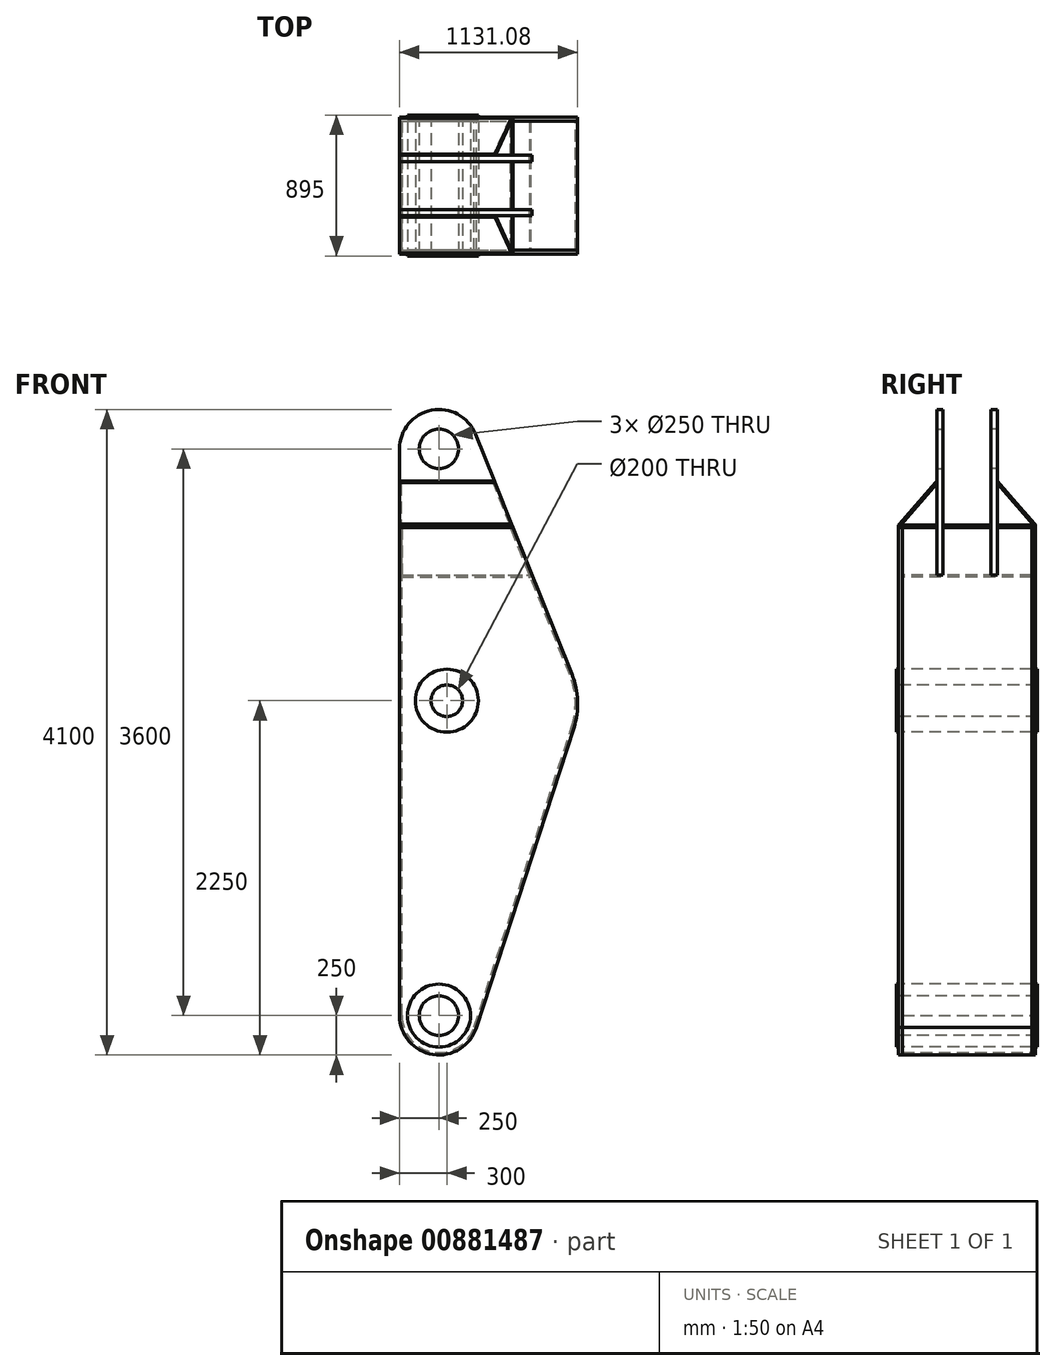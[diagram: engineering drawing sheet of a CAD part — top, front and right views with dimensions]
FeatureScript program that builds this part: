
annotation { "Feature Type Name" : "Feature", "Feature Type Description" : "" }
export const myFeature = defineFeature(function(context is Context, id is Id, definition is map)
    precondition{}
    {
        {
            var Q0;
            Q0=qCreatedBy(makeId("Front.planeOp"),FACE);
            var sketch = newSketch(context, id + "F0", { "sketchPlane" : qUnion([Q0])});
            skArc(sketch, "E0", {"start": v(-250, 0) * mm, "mid": v(-37.8, -247.13) * mm, "end": v(238.57, -74.73) * mm});
            skCircle(sketch, "E1", {"center": v(0, 0) * mm, "radius": 125 * mm});
            skCircle(sketch, "E2", {"center": v(0, 0) * mm, "radius": 200 * mm});
            skLineSegment(sketch, "E3", {"start": v(-250, 0) * mm, "end": v(-250, 3600) * mm});
            skCircle(sketch, "E4", {"center": v(0, 3600) * mm, "radius": 125 * mm});
            skLineSegment(sketch, "E5", {"start": v(238.57, -74.73) * mm, "end": v(856.6, 1827.38) * mm});
            skLineSegment(sketch, "E6", {"start": v(844.99, 2168.4) * mm, "end": v(231.96, 3693.25) * mm});
            skCircle(sketch, "E7", {"center": v(50, 2000) * mm, "radius": 100 * mm});
            skCircle(sketch, "E8", {"center": v(50, 2000) * mm, "radius": 200 * mm});
            skPoint(sketch, "E9.visualSharp", {"position": v(912.7, 2000) * mm});
            skArc(sketch, "E9.filletArc", {"start": v(856.6, 1827.38) * mm, "mid": v(880.79, 1998.91) * mm, "end": v(844.99, 2168.4) * mm});
            skArc(sketch, "E10", {"start": v(231.96, 3693.25) * mm, "mid": v(-47.5, 3845.45) * mm, "end": v(-250, 3600) * mm});
            skLineSegment(sketch, "E11", {"start": v(-250, 3100) * mm, "end": v(470.46, 3100) * mm});
            skLineSegment(sketch, "E12", {"start": v(-250, 2800) * mm, "end": v(591.07, 2800) * mm});
            skSolve(sketch);
        }
        {
            var Q0;
            {var subQ1=sQuery(id+"F0.wireOp",EDGE,"E0");Q0=makeQuery(id+"F0.imprint","IMPRINT",FACE,{"disambiguationData":[TD([[makeQuery(id+"F0.imprint","IMPRINT",EDGE,{"derivedFrom":subQ1}),1.0]])]});}
            var Q1;
            {var subQ0=sQuery(id+"F0.wireOp",EDGE,"E11");Q1=makeQuery(id+"F0.imprint","IMPRINT",FACE,{"disambiguationData":[TD([[makeQuery(id+"F0.imprint","IMPRINT",EDGE,{"derivedFrom":subQ0}),-1.0]])]});}
            extrude(context, id + "F1", {"entities" : qUnion([Q0, Q1]), "depth" : 25 * mm, "offsetDistance" : 25 * mm, "symmetric" : true});
        }
        {
            var Q0;
            Q0=makeQuery(id+"F1.opExtrude","CAP_FACE",FACE,{"disambiguationData":[OSD([sQuery(id+"F0.wireOp",EDGE,"E0"),sQuery(id+"F0.wireOp",EDGE,"E2"),sQuery(id+"F0.wireOp",EDGE,"E3"),sQuery(id+"F0.wireOp",EDGE,"E5"),sQuery(id+"F0.wireOp",EDGE,"E6"),sQuery(id+"F0.wireOp",EDGE,"E8"),sQuery(id+"F0.wireOp",EDGE,"E9.filletArc"),sQuery(id+"F0.wireOp",EDGE,"E11")])],"isStart":true});
            cPlane(context, id + "F2", {"entities" : qUnion([Q0]), "cplaneType" : CPlaneType.OFFSET, "offset" : 410 * mm, "width" : 150 * mm, "height" : 150 * mm});
        }
        {
            var Q0;
            Q0=makeQuery(id+"F1.opExtrude","SWEPT_BODY",BODY,{"disambiguationData":[OSD([sQuery(id+"F0.wireOp",EDGE,"E0"),sQuery(id+"F0.wireOp",EDGE,"E2"),sQuery(id+"F0.wireOp",EDGE,"E3"),sQuery(id+"F0.wireOp",EDGE,"E5"),sQuery(id+"F0.wireOp",EDGE,"E6"),sQuery(id+"F0.wireOp",EDGE,"E8"),sQuery(id+"F0.wireOp",EDGE,"E9.filletArc"),sQuery(id+"F0.wireOp",EDGE,"E11")])]});
            var Q1;
            Q1=qCreatedBy(id+"F2.planeOp",FACE);
            mirror(context, id + "F3", {"entities" : qUnion([Q0]), "mirrorPlane" : qUnion([Q1])});
        }
        {
            var Q0;
            Q0=makeQuery(id+"F3.opPattern","COPY",FACE,{"derivedFrom":makeQuery(id+"F1.opExtrude","CAP_FACE",FACE,{"disambiguationData":[OSD([sQuery(id+"F0.wireOp",EDGE,"E0"),sQuery(id+"F0.wireOp",EDGE,"E2"),sQuery(id+"F0.wireOp",EDGE,"E3"),sQuery(id+"F0.wireOp",EDGE,"E5"),sQuery(id+"F0.wireOp",EDGE,"E6"),sQuery(id+"F0.wireOp",EDGE,"E8"),sQuery(id+"F0.wireOp",EDGE,"E9.filletArc"),sQuery(id+"F0.wireOp",EDGE,"E11")])],"isStart":true}),"instanceName":"1"});
            var Q1;
            Q1=makeQuery(id+"F3.opPattern","COPY",FACE,{"derivedFrom":makeQuery(id+"F1.opExtrude","CAP_FACE",FACE,{"disambiguationData":[OSD([sQuery(id+"F0.wireOp",EDGE,"E0"),sQuery(id+"F0.wireOp",EDGE,"E2"),sQuery(id+"F0.wireOp",EDGE,"E3"),sQuery(id+"F0.wireOp",EDGE,"E5"),sQuery(id+"F0.wireOp",EDGE,"E6"),sQuery(id+"F0.wireOp",EDGE,"E8"),sQuery(id+"F0.wireOp",EDGE,"E9.filletArc"),sQuery(id+"F0.wireOp",EDGE,"E11")])],"isStart":false}),"instanceName":"1"});
            cPlane(context, id + "F4", {"entities" : qUnion([Q0, Q1]), "cplaneType" : CPlaneType.MID_PLANE, "offset" : 25 * mm, "width" : 150 * mm, "height" : 150 * mm});
        }
        {
            var Q0;
            Q0=makeQuery(id+"F0.imprint","IMPRINT",FACE,{"disambiguationData":[TD([[makeQuery(id+"F0.imprint","IMPRINT",EDGE,{"derivedFrom":sQuery(id+"F0.wireOp",EDGE,"E7")}),-1.0]])]});
            var Q1;
            Q1=makeQuery(id+"F0.imprint","IMPRINT",FACE,{"disambiguationData":[TD([[makeQuery(id+"F0.imprint","IMPRINT",EDGE,{"derivedFrom":sQuery(id+"F0.wireOp",EDGE,"E1")}),-1.0]])]});
            var Q2;
            Q2=qCreatedBy(id+"F4.planeOp",FACE);
            extrude(context, id + "F5", {"entities" : qUnion([Q0, Q1]), "endBound" : BoundingType.UP_TO_SURFACE, "oppositeDirection" : true, "depth" : 25 * mm, "endBoundEntityFace" : qUnion([Q2]), "offsetDistance" : 25 * mm});
        }
        {
            var Q0;
            Q0=makeQuery(id+"F0.imprint","IMPRINT",FACE,{"disambiguationData":[TD([[makeQuery(id+"F0.imprint","IMPRINT",EDGE,{"derivedFrom":sQuery(id+"F0.wireOp",EDGE,"E7")}),-1.0]])]});
            extrude(context, id + "F6", {"entities" : qUnion([Q0]), "operationType" : NewBodyOperationType.ADD, "depth" : 25 * mm, "offsetDistance" : 25 * mm});
        }
        {
            var Q0;
            Q0=makeQuery(id+"F5.opExtrude","CAP_FACE",FACE,{"disambiguationData":[OSD([sQuery(id+"F0.wireOp",EDGE,"E7"),sQuery(id+"F0.wireOp",EDGE,"E8")])],"isStart":false});
            extrude(context, id + "F7", {"entities" : qUnion([Q0]), "operationType" : NewBodyOperationType.ADD, "depth" : 25 * mm, "offsetDistance" : 25 * mm});
        }
        {
            var Q0;
            Q0=makeQuery(id+"F0.imprint","IMPRINT",FACE,{"disambiguationData":[TD([[makeQuery(id+"F0.imprint","IMPRINT",EDGE,{"derivedFrom":sQuery(id+"F0.wireOp",EDGE,"E1")}),-1.0]])]});
            extrude(context, id + "F8", {"entities" : qUnion([Q0]), "operationType" : NewBodyOperationType.ADD, "depth" : 25 * mm, "offsetDistance" : 25 * mm});
        }
        {
            var Q0;
            Q0=makeQuery(id+"F5.opExtrude","CAP_FACE",FACE,{"disambiguationData":[OSD([sQuery(id+"F0.wireOp",EDGE,"E1"),sQuery(id+"F0.wireOp",EDGE,"E2")])],"isStart":false});
            extrude(context, id + "F9", {"entities" : qUnion([Q0]), "operationType" : NewBodyOperationType.ADD, "depth" : 25 * mm, "offsetDistance" : 25 * mm});
        }
        {
            var Q0;
            Q0=makeQuery(id+"F0.imprint","IMPRINT",FACE,{"disambiguationData":[TD([[makeQuery(id+"F0.imprint","IMPRINT",EDGE,{"derivedFrom":sQuery(id+"F0.wireOp",EDGE,"E4")}),-1.0]])]});
            var Q1;
            {var subQ0=sQuery(id+"F0.wireOp",EDGE,"E11");Q1=makeQuery(id+"F0.imprint","IMPRINT",FACE,{"disambiguationData":[TD([[makeQuery(id+"F0.imprint","IMPRINT",EDGE,{"derivedFrom":subQ0}),-1.0]])]});}
            extrude(context, id + "F10", {"entities" : qUnion([Q0, Q1]), "depth" : 40 * mm, "offsetDistance" : 25 * mm, "symmetric" : true});
        }
        {
            var Q0;
            Q0=makeQuery(id+"F10.opExtrude","SWEPT_BODY",BODY,{"disambiguationData":[OSD([sQuery(id+"F0.wireOp",EDGE,"E3"),sQuery(id+"F0.wireOp",EDGE,"E4"),sQuery(id+"F0.wireOp",EDGE,"E6"),sQuery(id+"F0.wireOp",EDGE,"E10"),sQuery(id+"F0.wireOp",EDGE,"E12")])]});
            transform(context, id + "F11", {"entities" : qUnion([Q0]), "transformType" : TransformType.TRANSLATION_3D, "dx" : 0 * mm, "dy" : 250 * mm, "dz" : 0 * mm, "makeCopy" : false});
        }
        {
            var Q0;
            Q0=makeQuery(id+"F10.opExtrude","SWEPT_BODY",BODY,{"disambiguationData":[OSD([sQuery(id+"F0.wireOp",EDGE,"E3"),sQuery(id+"F0.wireOp",EDGE,"E4"),sQuery(id+"F0.wireOp",EDGE,"E6"),sQuery(id+"F0.wireOp",EDGE,"E10"),sQuery(id+"F0.wireOp",EDGE,"E12")])]});
            var Q1;
            Q1=qCreatedBy(id+"F2.planeOp",FACE);
            mirror(context, id + "F12", {"entities" : qUnion([Q0]), "mirrorPlane" : qUnion([Q1])});
        }
        {
            var Q0;
            Q0=makeQuery(id+"F1.opExtrude","CAP_FACE",FACE,{"disambiguationData":[OSD([sQuery(id+"F0.wireOp",EDGE,"E0"),sQuery(id+"F0.wireOp",EDGE,"E2"),sQuery(id+"F0.wireOp",EDGE,"E3"),sQuery(id+"F0.wireOp",EDGE,"E5"),sQuery(id+"F0.wireOp",EDGE,"E6"),sQuery(id+"F0.wireOp",EDGE,"E8"),sQuery(id+"F0.wireOp",EDGE,"E9.filletArc"),sQuery(id+"F0.wireOp",EDGE,"E11")])],"isStart":false});
            var sketch = newSketch(context, id + "F13", { "sketchPlane" : qUnion([Q0])});
            skLineSegment(sketch, "E13.0", {"start": v(-250, 3100) * mm, "end": v(470.46, 3100) * mm});
            skLineSegment(sketch, "E14.0", {"start": v(-250, 3115) * mm, "end": v(464.43, 3115) * mm});
            skLineSegment(sketch, "E15", {"start": v(-250, 3115) * mm, "end": v(-250, 3100) * mm});
            skLineSegment(sketch, "E16.0", {"start": v(470.46, 3100) * mm, "end": v(464.43, 3115) * mm});
            skPoint(sketch, "E17.orphan", {"position": v(231.96, 3693.25) * mm});
            skPoint(sketch, "E18.orphan", {"position": v(591.07, 2800) * mm});
            skSolve(sketch);
        }
        {
            var Q0;
            Q0=makeQuery(id+"F13.imprint","IMPRINT",FACE,{"disambiguationData":[TD([[makeQuery(id+"F13.imprint","IMPRINT",EDGE,{"derivedFrom":sQuery(id+"F13.wireOp",EDGE,"E13.0")}),1.0]])]});
            var Q1;
            Q1=makeQuery(id+"F3.opPattern","COPY",FACE,{"derivedFrom":makeQuery(id+"F1.opExtrude","CAP_FACE",FACE,{"disambiguationData":[OSD([sQuery(id+"F0.wireOp",EDGE,"E0"),sQuery(id+"F0.wireOp",EDGE,"E2"),sQuery(id+"F0.wireOp",EDGE,"E3"),sQuery(id+"F0.wireOp",EDGE,"E5"),sQuery(id+"F0.wireOp",EDGE,"E6"),sQuery(id+"F0.wireOp",EDGE,"E8"),sQuery(id+"F0.wireOp",EDGE,"E9.filletArc"),sQuery(id+"F0.wireOp",EDGE,"E11")])],"isStart":false}),"instanceName":"1"});
            var Q2;
            Q2=makeQuery(id+"F3.opPattern","COPY",BODY,{"derivedFrom":makeQuery(id+"F1.opExtrude","SWEPT_BODY",BODY,{"disambiguationData":[OSD([sQuery(id+"F0.wireOp",EDGE,"E0"),sQuery(id+"F0.wireOp",EDGE,"E2"),sQuery(id+"F0.wireOp",EDGE,"E3"),sQuery(id+"F0.wireOp",EDGE,"E5"),sQuery(id+"F0.wireOp",EDGE,"E6"),sQuery(id+"F0.wireOp",EDGE,"E8"),sQuery(id+"F0.wireOp",EDGE,"E9.filletArc"),sQuery(id+"F0.wireOp",EDGE,"E11")])]}),"instanceName":"1"});
            var Q3;
            Q3=makeQuery(id+"F3.opPattern","COPY",VERTEX,{"derivedFrom":makeQuery(id+"F1.opExtrude","CAP_VERTEX",VERTEX,{"disambiguationData":[OSD([sQuery(id+"F0.wireOp",EDGE,"E6"),sQuery(id+"F0.wireOp",EDGE,"E11")])],"isStart":false}),"instanceName":"1"});
            extrude(context, id + "F14", {"entities" : qUnion([Q0]), "endBound" : BoundingType.UP_TO_VERTEX, "oppositeDirection" : true, "depth" : 25 * mm, "endBoundEntityFace" : qUnion([Q1]), "endBoundEntityBody" : qUnion([Q2]), "endBoundEntityVertex" : qUnion([Q3]), "offsetDistance" : 25 * mm});
        }
        {
            var Q0;
            Q0=makeQuery(id+"F10.opExtrude","SWEPT_BODY",BODY,{"disambiguationData":[OSD([sQuery(id+"F0.wireOp",EDGE,"E3"),sQuery(id+"F0.wireOp",EDGE,"E4"),sQuery(id+"F0.wireOp",EDGE,"E6"),sQuery(id+"F0.wireOp",EDGE,"E10"),sQuery(id+"F0.wireOp",EDGE,"E12")])]});
            var Q1;
            Q1=makeQuery(id+"F12.opPattern","COPY",BODY,{"derivedFrom":makeQuery(id+"F10.opExtrude","SWEPT_BODY",BODY,{"disambiguationData":[OSD([sQuery(id+"F0.wireOp",EDGE,"E3"),sQuery(id+"F0.wireOp",EDGE,"E4"),sQuery(id+"F0.wireOp",EDGE,"E6"),sQuery(id+"F0.wireOp",EDGE,"E10"),sQuery(id+"F0.wireOp",EDGE,"E12")])]}),"instanceName":"1"});
            var Q2;
            Q2=makeQuery(id+"F14.opExtrude","SWEPT_BODY",BODY,{"disambiguationData":[OSD([sQuery(id+"F13.wireOp",EDGE,"E13.0"),sQuery(id+"F13.wireOp",EDGE,"E14.0"),sQuery(id+"F13.wireOp",EDGE,"E15"),sQuery(id+"F13.wireOp",EDGE,"E16.0")])]});
            booleanBodies(context, id + "F15", {"operationType" : BooleanOperationType.SUBTRACTION, "tools" : qUnion([Q0, Q1]), "targets" : qUnion([Q2]), "keepTools" : true});
        }
        {
            var Q0;
            Q0=makeQuery(id+"F3.opPattern","COPY",FACE,{"derivedFrom":makeQuery(id+"F1.opExtrude","CAP_FACE",FACE,{"disambiguationData":[OSD([sQuery(id+"F0.wireOp",EDGE,"E0"),sQuery(id+"F0.wireOp",EDGE,"E2"),sQuery(id+"F0.wireOp",EDGE,"E3"),sQuery(id+"F0.wireOp",EDGE,"E5"),sQuery(id+"F0.wireOp",EDGE,"E6"),sQuery(id+"F0.wireOp",EDGE,"E8"),sQuery(id+"F0.wireOp",EDGE,"E9.filletArc"),sQuery(id+"F0.wireOp",EDGE,"E11")])],"isStart":true}),"instanceName":"1"});
            var sketch = newSketch(context, id + "F16", { "sketchPlane" : qUnion([Q0])});
            skLineSegment(sketch, "E19.0", {"start": v(844.99, 2168.4) * mm, "end": v(470.46, 3100) * mm});
            skLineSegment(sketch, "E20.0", {"start": v(-250, 3100) * mm, "end": v(-235, 3100) * mm});
            skArc(sketch, "E21.0", {"start": v(856.6, 1827.38) * mm, "mid": v(880.79, 1998.91) * mm, "end": v(844.99, 2168.4) * mm});
            skLineSegment(sketch, "E22.0", {"start": v(238.57, -74.73) * mm, "end": v(856.6, 1827.38) * mm});
            skArc(sketch, "E23.0", {"start": v(-250, 0) * mm, "mid": v(-37.8, -247.13) * mm, "end": v(238.57, -74.73) * mm});
            skLineSegment(sketch, "E24.0", {"start": v(-250, 0) * mm, "end": v(-250, 3100) * mm});
            skPoint(sketch, "E25.orphan", {"position": v(-250, 3600) * mm});
            skPoint(sketch, "E26.orphan", {"position": v(231.96, 3693.25) * mm});
            skLineSegment(sketch, "E27.0", {"start": v(831.07, 2162.8) * mm, "end": v(454.3, 3100) * mm});
            skLineSegment(sketch, "E27.1", {"start": v(-235, 0) * mm, "end": v(-235, 3100) * mm});
            skArc(sketch, "E27.2", {"start": v(-235, 0) * mm, "mid": v(-35.5, -232.3) * mm, "end": v(224.28, -70.17) * mm});
            skLineSegment(sketch, "E27.3", {"start": v(224.28, -70.17) * mm, "end": v(842.34, 1832.02) * mm});
            skArc(sketch, "E27.4", {"start": v(842.34, 1832.02) * mm, "mid": v(865.8, 1998.4) * mm, "end": v(831.07, 2162.8) * mm});
            skLineSegment(sketch, "E28.trimOffspring", {"start": v(454.3, 3100) * mm, "end": v(470.46, 3100) * mm});
            skLineSegment(sketch, "E29", {"start": v(-250, 0) * mm, "end": v(-235, 0) * mm});
            skLineSegment(sketch, "E30", {"start": v(224.28, -70.17) * mm, "end": v(238.57, -74.73) * mm});
            skLineSegment(sketch, "E31", {"start": v(842.34, 1832.02) * mm, "end": v(856.6, 1827.38) * mm});
            skLineSegment(sketch, "E32", {"start": v(831.07, 2162.8) * mm, "end": v(844.99, 2168.4) * mm});
            skSolve(sketch);
        }
        {
            var Q0;
            Q0=makeQuery(id+"F16.imprint","IMPRINT",FACE,{"disambiguationData":[TD([[makeQuery(id+"F16.imprint","IMPRINT",EDGE,{"derivedFrom":sQuery(id+"F16.wireOp",EDGE,"E20.0")}),-1.0]])]});
            var Q1;
            Q1=makeQuery(id+"F16.imprint","IMPRINT",FACE,{"disambiguationData":[TD([[makeQuery(id+"F16.imprint","IMPRINT",EDGE,{"derivedFrom":sQuery(id+"F16.wireOp",EDGE,"E19.0")}),1.0]])]});
            var Q2;
            Q2=makeQuery(id+"F16.imprint","IMPRINT",FACE,{"disambiguationData":[TD([[makeQuery(id+"F16.imprint","IMPRINT",EDGE,{"derivedFrom":sQuery(id+"F16.wireOp",EDGE,"E22.0")}),1.0]])]});
            var Q3;
            Q3=makeQuery(id+"F16.imprint","IMPRINT",FACE,{"disambiguationData":[TD([[makeQuery(id+"F16.imprint","IMPRINT",EDGE,{"derivedFrom":sQuery(id+"F16.wireOp",EDGE,"E21.0")}),1.0]])]});
            extrude(context, id + "F17", {"entities" : qUnion([Q0, Q1, Q2, Q3]), "endBound" : BoundingType.UP_TO_NEXT, "depth" : 25 * mm, "offsetDistance" : 25 * mm});
        }
        {
            var Q0;
            Q0=makeQuery(id+"F16.imprint","IMPRINT",FACE,{"disambiguationData":[TD([[makeQuery(id+"F16.imprint","IMPRINT",EDGE,{"derivedFrom":sQuery(id+"F16.wireOp",EDGE,"E23.0")}),1.0]])]});
            extrude(context, id + "F18", {"entities" : qUnion([Q0]), "endBound" : BoundingType.UP_TO_NEXT, "depth" : 25 * mm, "offsetDistance" : 25 * mm});
        }
        {
            var Q0;
            Q0=makeQuery(id+"F1.opExtrude","CAP_FACE",FACE,{"disambiguationData":[OSD([sQuery(id+"F0.wireOp",EDGE,"E0"),sQuery(id+"F0.wireOp",EDGE,"E2"),sQuery(id+"F0.wireOp",EDGE,"E3"),sQuery(id+"F0.wireOp",EDGE,"E5"),sQuery(id+"F0.wireOp",EDGE,"E6"),sQuery(id+"F0.wireOp",EDGE,"E8"),sQuery(id+"F0.wireOp",EDGE,"E9.filletArc"),sQuery(id+"F0.wireOp",EDGE,"E11")])],"isStart":true});
            var sketch = newSketch(context, id + "F19", { "sketchPlane" : qUnion([Q0])});
            skLineSegment(sketch, "E33.0", {"start": v(235, 2800) * mm, "end": v(-574.9, 2800) * mm});
            skLineSegment(sketch, "E34.0", {"start": v(235, 2785) * mm, "end": v(-580.93, 2785) * mm});
            skArc(sketch, "E35.0.0", {"start": v(-856.6, 1827.38) * mm, "mid": v(-880.79, 1998.91) * mm, "end": v(-844.99, 2168.4) * mm});
            skLineSegment(sketch, "E35.0.1", {"start": v(-844.99, 2168.4) * mm, "end": v(-470.46, 3100) * mm});
            skLineSegment(sketch, "E35.0.2", {"start": v(-470.46, 3100) * mm, "end": v(250, 3100) * mm});
            skLineSegment(sketch, "E35.0.3", {"start": v(250, 3100) * mm, "end": v(250, 0) * mm});
            skArc(sketch, "E35.0.4", {"start": v(250, 0) * mm, "mid": v(37.8, -247.13) * mm, "end": v(-238.57, -74.73) * mm});
            skLineSegment(sketch, "E35.0.5", {"start": v(-238.57, -74.73) * mm, "end": v(-856.6, 1827.38) * mm});
            skPoint(sketch, "E36.orphan", {"position": v(-844.99, 2168.4) * mm});
            skLineSegment(sketch, "E37.0", {"start": v(235, 0) * mm, "end": v(235, 2800) * mm});
            skLineSegment(sketch, "E38.0", {"start": v(-831.07, 2162.8) * mm, "end": v(-454.3, 3100) * mm});
            skPoint(sketch, "E39.orphan", {"position": v(235, 3100) * mm});
            skPoint(sketch, "E40.orphan", {"position": v(250, 2800) * mm});
            skSolve(sketch);
        }
        {
            var Q0;
            {var subQ0=sQuery(id+"F19.wireOp",EDGE,"E33.0");Q0=makeQuery(id+"F19.imprint","IMPRINT",FACE,{"disambiguationData":[TD([[makeQuery(id+"F19.imprint","IMPRINT",EDGE,{"derivedFrom":subQ0}),1.0]])]});}
            var Q1;
            Q1=makeQuery(id+"F3.opPattern","COPY",FACE,{"derivedFrom":makeQuery(id+"F1.opExtrude","CAP_FACE",FACE,{"disambiguationData":[OSD([sQuery(id+"F0.wireOp",EDGE,"E0"),sQuery(id+"F0.wireOp",EDGE,"E2"),sQuery(id+"F0.wireOp",EDGE,"E3"),sQuery(id+"F0.wireOp",EDGE,"E5"),sQuery(id+"F0.wireOp",EDGE,"E6"),sQuery(id+"F0.wireOp",EDGE,"E8"),sQuery(id+"F0.wireOp",EDGE,"E9.filletArc"),sQuery(id+"F0.wireOp",EDGE,"E11")])],"isStart":true}),"instanceName":"1"});
            extrude(context, id + "F20", {"entities" : qUnion([Q0]), "endBound" : BoundingType.UP_TO_SURFACE, "depth" : 25 * mm, "endBoundEntityFace" : qUnion([Q1]), "offsetDistance" : 25 * mm});
        }
        {
            var Q0;
            Q0=makeQuery(id+"F10.opExtrude","SWEPT_BODY",BODY,{"disambiguationData":[OSD([sQuery(id+"F0.wireOp",EDGE,"E3"),sQuery(id+"F0.wireOp",EDGE,"E4"),sQuery(id+"F0.wireOp",EDGE,"E6"),sQuery(id+"F0.wireOp",EDGE,"E10"),sQuery(id+"F0.wireOp",EDGE,"E12")])]});
            var Q1;
            Q1=makeQuery(id+"F12.opPattern","COPY",BODY,{"derivedFrom":makeQuery(id+"F10.opExtrude","SWEPT_BODY",BODY,{"disambiguationData":[OSD([sQuery(id+"F0.wireOp",EDGE,"E3"),sQuery(id+"F0.wireOp",EDGE,"E4"),sQuery(id+"F0.wireOp",EDGE,"E6"),sQuery(id+"F0.wireOp",EDGE,"E10"),sQuery(id+"F0.wireOp",EDGE,"E12")])]}),"instanceName":"1"});
            var Q2;
            Q2=makeQuery(id+"F17.opExtrude","SWEPT_BODY",BODY,{"disambiguationData":[OSD([sQuery(id+"F16.wireOp",EDGE,"E19.0"),sQuery(id+"F16.wireOp",EDGE,"E21.0"),sQuery(id+"F16.wireOp",EDGE,"E22.0"),sQuery(id+"F16.wireOp",EDGE,"E27.0"),sQuery(id+"F16.wireOp",EDGE,"E27.3"),sQuery(id+"F16.wireOp",EDGE,"E27.4"),sQuery(id+"F16.wireOp",EDGE,"E28.trimOffspring"),sQuery(id+"F16.wireOp",EDGE,"E30")])]});
            booleanBodies(context, id + "F21", {"operationType" : BooleanOperationType.SUBTRACTION, "tools" : qUnion([Q0, Q1]), "targets" : qUnion([Q2]), "keepTools" : true});
        }
        {
            var Q0;
            Q0=makeQuery(id+"F12.opPattern","COPY",BODY,{"derivedFrom":makeQuery(id+"F10.opExtrude","SWEPT_BODY",BODY,{"disambiguationData":[OSD([sQuery(id+"F0.wireOp",EDGE,"E3"),sQuery(id+"F0.wireOp",EDGE,"E4"),sQuery(id+"F0.wireOp",EDGE,"E6"),sQuery(id+"F0.wireOp",EDGE,"E10"),sQuery(id+"F0.wireOp",EDGE,"E12")])]}),"instanceName":"1"});
            var Q1;
            Q1=makeQuery(id+"F10.opExtrude","SWEPT_BODY",BODY,{"disambiguationData":[OSD([sQuery(id+"F0.wireOp",EDGE,"E3"),sQuery(id+"F0.wireOp",EDGE,"E4"),sQuery(id+"F0.wireOp",EDGE,"E6"),sQuery(id+"F0.wireOp",EDGE,"E10"),sQuery(id+"F0.wireOp",EDGE,"E12")])]});
            var Q2;
            Q2=makeQuery(id+"F17.opExtrude","SWEPT_BODY",BODY,{"disambiguationData":[OSD([sQuery(id+"F16.wireOp",EDGE,"E20.0"),sQuery(id+"F16.wireOp",EDGE,"E24.0"),sQuery(id+"F16.wireOp",EDGE,"E27.1"),sQuery(id+"F16.wireOp",EDGE,"E29")])]});
            booleanBodies(context, id + "F22", {"operationType" : BooleanOperationType.SUBTRACTION, "tools" : qUnion([Q0, Q1]), "targets" : qUnion([Q2]), "keepTools" : true});
        }
        {
            var Q0;
            Q0=makeQuery(id+"F10.opExtrude","SWEPT_FACE",FACE,{"disambiguationData":[OSD([sQuery(id+"F0.wireOp",EDGE,"E3")])]});
            var sketch = newSketch(context, id + "F23", { "sketchPlane" : qUnion([Q0])});
            skLineSegment(sketch, "E41", {"start": v(-230, 3395) * mm, "end": v(12.5, 3115) * mm});
            skLineSegment(sketch, "E42.0", {"start": v(-230, 3379.73) * mm, "end": v(-0.73, 3115) * mm});
            skLineSegment(sketch, "E43.0", {"start": v(-0.73, 3115) * mm, "end": v(12.5, 3115) * mm});
            skLineSegment(sketch, "E44.trimOffspring", {"start": v(-230, 3379.73) * mm, "end": v(-230, 3395) * mm});
            skLineSegment(sketch, "E45", {"start": v(-230, 3379.73) * mm, "end": v(-222.44, 3386.27) * mm});
            skLineSegment(sketch, "E46", {"start": v(-0.73, 3115) * mm, "end": v(6.83, 3121.55) * mm});
            skSolve(sketch);
        }
        {
            var Q0;
            Q0=makeQuery(id+"F23.imprint","IMPRINT",FACE,{"disambiguationData":[TD([[makeQuery(id+"F23.imprint","IMPRINT",EDGE,{"derivedFrom":sQuery(id+"F23.wireOp",EDGE,"E42.0")}),1.0]])]});
            var Q1;
            Q1=sQuery(id+"F13.wireOp",VERTEX,"E14.0.end");
            extrude(context, id + "F24", {"entities" : qUnion([Q0]), "endBound" : BoundingType.UP_TO_VERTEX, "oppositeDirection" : true, "depth" : 25 * mm, "endBoundEntityVertex" : qUnion([Q1]), "offsetDistance" : 25 * mm});
        }
        {
            var Q0;
            {var subQ0=sQuery(id+"F23.wireOp",EDGE,"E44.trimOffspring");Q0=makeQuery(id+"F23.imprint","IMPRINT",FACE,{"disambiguationData":[TD([[makeQuery(id+"F23.imprint","IMPRINT",EDGE,{"derivedFrom":subQ0}),-1.0]])]});}
            var Q1;
            {var subQ0=sQuery(id+"F23.wireOp",EDGE,"E43.0");Q1=makeQuery(id+"F23.imprint","IMPRINT",FACE,{"disambiguationData":[TD([[makeQuery(id+"F23.imprint","IMPRINT",EDGE,{"derivedFrom":subQ0}),1.0]])]});}
            var Q2;
            Q2=makeQuery(id+"F24.opExtrude","CAP_FACE",FACE,{"disambiguationData":[OSD([sQuery(id+"F23.wireOp",EDGE,"E41"),sQuery(id+"F23.wireOp",EDGE,"E42.0"),sQuery(id+"F23.wireOp",EDGE,"E45"),sQuery(id+"F23.wireOp",EDGE,"E46")])],"isStart":false});
            extrude(context, id + "F25", {"entities" : qUnion([Q0, Q1]), "endBound" : BoundingType.UP_TO_SURFACE, "oppositeDirection" : true, "depth" : 25 * mm, "endBoundEntityFace" : qUnion([Q2]), "offsetDistance" : 25 * mm});
        }
        {
            var Q0;
            Q0=makeQuery(id+"F12.opPattern","COPY",VERTEX,{"derivedFrom":makeQuery(id+"F10.opExtrude","CAP_VERTEX",VERTEX,{"disambiguationData":[OSD([sQuery(id+"F0.wireOp",EDGE,"E6"),sQuery(id+"F0.wireOp",EDGE,"E10")])],"isStart":true}),"instanceName":"1"});
            var Q1;
            Q1=makeQuery(id+"F12.opPattern","COPY",VERTEX,{"derivedFrom":makeQuery(id+"F10.opExtrude","CAP_VERTEX",VERTEX,{"disambiguationData":[OSD([sQuery(id+"F0.wireOp",EDGE,"E6"),sQuery(id+"F0.wireOp",EDGE,"E10")])],"isStart":false}),"instanceName":"1"});
            var Q2;
            Q2=makeQuery(id+"F12.opPattern","COPY",VERTEX,{"derivedFrom":makeQuery(id+"F10.opExtrude","CAP_VERTEX",VERTEX,{"disambiguationData":[OSD([sQuery(id+"F0.wireOp",EDGE,"E6"),sQuery(id+"F0.wireOp",EDGE,"E12")])],"isStart":false}),"instanceName":"1"});
            cPlane(context, id + "F26", {"entities" : qUnion([Q0, Q1, Q2]), "cplaneType" : CPlaneType.THREE_POINT, "offset" : 25 * mm, "width" : 150 * mm, "height" : 150 * mm});
        }
        {
            var Q0;
            Q0=makeQuery(id+"F10.opExtrude","CAP_FACE",FACE,{"disambiguationData":[OSD([sQuery(id+"F0.wireOp",EDGE,"E3"),sQuery(id+"F0.wireOp",EDGE,"E4"),sQuery(id+"F0.wireOp",EDGE,"E6"),sQuery(id+"F0.wireOp",EDGE,"E10"),sQuery(id+"F0.wireOp",EDGE,"E12")])],"isStart":false});
            var sketch = newSketch(context, id + "F27", { "sketchPlane" : qUnion([Q0])});
            skLineSegment(sketch, "E47.0", {"start": v(591.07, 2800) * mm, "end": v(231.96, 3693.25) * mm});
            skLineSegment(sketch, "E48", {"start": v(231.96, 3693.25) * mm, "end": v(575.62, 3460.53) * mm});
            skLineSegment(sketch, "E49", {"start": v(575.62, 3460.53) * mm, "end": v(591.07, 2800) * mm});
            skSolve(sketch);
        }
        {
            var Q0;
            Q0=makeQuery(id+"F27.imprint","IMPRINT",FACE,{"disambiguationData":[TD([[makeQuery(id+"F27.imprint","IMPRINT",EDGE,{"derivedFrom":sQuery(id+"F27.wireOp",EDGE,"E47.0")}),-1.0]])]});
            extrude(context, id + "F28", {"entities" : qUnion([Q0]), "depth" : 404 * mm, "offsetDistance" : 25 * mm});
        }
        {
            var Q0;
            Q0=makeQuery(id+"F28.opExtrude","SWEPT_BODY",BODY,{"disambiguationData":[OSD([sQuery(id+"F27.wireOp",EDGE,"E47.0"),sQuery(id+"F27.wireOp",EDGE,"E48"),sQuery(id+"F27.wireOp",EDGE,"E49")])]});
            var Q1;
            Q1=makeQuery(id+"F25.opExtrude","SWEPT_BODY",BODY,{"disambiguationData":[OSD([sQuery(id+"F23.wireOp",EDGE,"E41"),sQuery(id+"F23.wireOp",EDGE,"E44.trimOffspring"),sQuery(id+"F23.wireOp",EDGE,"E45")])]});
            var Q2;
            Q2=makeQuery(id+"F25.opExtrude","SWEPT_BODY",BODY,{"disambiguationData":[OSD([sQuery(id+"F23.wireOp",EDGE,"E41"),sQuery(id+"F23.wireOp",EDGE,"E43.0"),sQuery(id+"F23.wireOp",EDGE,"E46")])]});
            var Q3;
            Q3=makeQuery(id+"F24.opExtrude","SWEPT_BODY",BODY,{"disambiguationData":[OSD([sQuery(id+"F23.wireOp",EDGE,"E41"),sQuery(id+"F23.wireOp",EDGE,"E42.0"),sQuery(id+"F23.wireOp",EDGE,"E45"),sQuery(id+"F23.wireOp",EDGE,"E46")])]});
            booleanBodies(context, id + "F29", {"operationType" : BooleanOperationType.SUBTRACTION, "tools" : qUnion([Q0]), "targets" : qUnion([Q1, Q2, Q3])});
        }
        {
            var Q0;
            {var subQ3=sQuery(id+"F23.wireOp",EDGE,"E44.trimOffspring");Q0=makeQuery(id+"F23.imprint","IMPRINT",FACE,{"disambiguationData":[TD([[makeQuery(id+"F23.imprint","IMPRINT",EDGE,{"derivedFrom":subQ3}),1.0]])]});}
            var sketch = newSketch(context, id + "F30", { "sketchPlane" : qUnion([Q0])});
            skLineSegment(sketch, "E50.0", {"start": v(-230, 3379.73) * mm, "end": v(-0.73, 3115) * mm});
            skLineSegment(sketch, "E51.0", {"start": v(-230, 3115) * mm, "end": v(-230, 3379.73) * mm});
            skLineSegment(sketch, "E52.0", {"start": v(-230, 3115) * mm, "end": v(-0.73, 3115) * mm});
            skPoint(sketch, "E53.orphan", {"position": v(-230, 2800) * mm});
            skPoint(sketch, "E54.orphan", {"position": v(12.5, 3115) * mm});
            skPoint(sketch, "E55.orphan", {"position": v(-230, 3600) * mm});
            skSolve(sketch);
        }
        {
            var Q0;
            Q0=makeQuery(id+"F30.imprint","IMPRINT",FACE,{"disambiguationData":[TD([[makeQuery(id+"F30.imprint","IMPRINT",EDGE,{"derivedFrom":sQuery(id+"F30.wireOp",EDGE,"E50.0")}),-1.0]])]});
            extrude(context, id + "F31", {"entities" : qUnion([Q0]), "oppositeDirection" : true, "depth" : 10 * mm, "offsetDistance" : 25 * mm});
        }
        {
            var Q0;
            Q0=qCreatedBy(id+"F26.planeOp",FACE);
            var sketch = newSketch(context, id + "F32", { "sketchPlane" : qUnion([Q0])});
            skLineSegment(sketch, "E56.0", {"start": v(230, 2716.94) * mm, "end": v(230, 3018.72) * mm});
            skLineSegment(sketch, "E57.0", {"start": v(-12.5, 2716.94) * mm, "end": v(230, 3018.72) * mm});
            skLineSegment(sketch, "E58.0", {"start": v(230, 2716.94) * mm, "end": v(-12.5, 2716.94) * mm});
            skPoint(sketch, "E59.orphan", {"position": v(230, 2377.44) * mm});
            skSolve(sketch);
        }
        {
            var Q0;
            Q0=makeQuery(id+"F32.imprint","IMPRINT",FACE,{"disambiguationData":[TD([[makeQuery(id+"F32.imprint","IMPRINT",EDGE,{"derivedFrom":sQuery(id+"F32.wireOp",EDGE,"E56.0")}),1.0]])]});
            extrude(context, id + "F33", {"entities" : qUnion([Q0]), "oppositeDirection" : true, "depth" : 10 * mm, "offsetDistance" : 25 * mm});
        }
        {
            var Q0;
            Q0=makeQuery(id+"F24.opExtrude","SWEPT_BODY",BODY,{"disambiguationData":[OSD([sQuery(id+"F23.wireOp",EDGE,"E41"),sQuery(id+"F23.wireOp",EDGE,"E42.0"),sQuery(id+"F23.wireOp",EDGE,"E45"),sQuery(id+"F23.wireOp",EDGE,"E46")])]});
            var Q1;
            Q1=makeQuery(id+"F25.opExtrude","SWEPT_BODY",BODY,{"disambiguationData":[OSD([sQuery(id+"F23.wireOp",EDGE,"E41"),sQuery(id+"F23.wireOp",EDGE,"E44.trimOffspring"),sQuery(id+"F23.wireOp",EDGE,"E45")])]});
            var Q2;
            Q2=makeQuery(id+"F25.opExtrude","SWEPT_BODY",BODY,{"disambiguationData":[OSD([sQuery(id+"F23.wireOp",EDGE,"E41"),sQuery(id+"F23.wireOp",EDGE,"E43.0"),sQuery(id+"F23.wireOp",EDGE,"E46")])]});
            var Q3;
            Q3=makeQuery(id+"F31.opExtrude","SWEPT_BODY",BODY,{"disambiguationData":[OSD([sQuery(id+"F30.wireOp",EDGE,"E50.0"),sQuery(id+"F30.wireOp",EDGE,"E51.0"),sQuery(id+"F30.wireOp",EDGE,"E52.0")])]});
            var Q4;
            Q4=makeQuery(id+"F33.opExtrude","SWEPT_BODY",BODY,{"disambiguationData":[OSD([sQuery(id+"F32.wireOp",EDGE,"E56.0"),sQuery(id+"F32.wireOp",EDGE,"E57.0"),sQuery(id+"F32.wireOp",EDGE,"E58.0")])]});
            var Q5;
            Q5=qCreatedBy(id+"F2.planeOp",FACE);
            mirror(context, id + "F34", {"entities" : qUnion([Q0, Q1, Q2, Q3, Q4]), "mirrorPlane" : qUnion([Q5])});
        }
        {
            var Q0;
            Q0=makeQuery(id+"F24.opExtrude","SWEPT_BODY",BODY,{"disambiguationData":[OSD([sQuery(id+"F23.wireOp",EDGE,"E41"),sQuery(id+"F23.wireOp",EDGE,"E42.0"),sQuery(id+"F23.wireOp",EDGE,"E45"),sQuery(id+"F23.wireOp",EDGE,"E46")])]});
            var Q1;
            Q1=makeQuery(id+"F25.opExtrude","SWEPT_BODY",BODY,{"disambiguationData":[OSD([sQuery(id+"F23.wireOp",EDGE,"E41"),sQuery(id+"F23.wireOp",EDGE,"E43.0"),sQuery(id+"F23.wireOp",EDGE,"E46")])]});
            var Q2;
            Q2=makeQuery(id+"F25.opExtrude","SWEPT_BODY",BODY,{"disambiguationData":[OSD([sQuery(id+"F23.wireOp",EDGE,"E41"),sQuery(id+"F23.wireOp",EDGE,"E44.trimOffspring"),sQuery(id+"F23.wireOp",EDGE,"E45")])]});
            var Q3;
            Q3=makeQuery(id+"F15.opBoolean","SPLIT",BODY,{"disambiguationData":[OD(0.0)],"derivedFrom":makeQuery(id+"F14.opExtrude","SWEPT_BODY",BODY,{"disambiguationData":[OSD([sQuery(id+"F13.wireOp",EDGE,"E13.0"),sQuery(id+"F13.wireOp",EDGE,"E14.0"),sQuery(id+"F13.wireOp",EDGE,"E15"),sQuery(id+"F13.wireOp",EDGE,"E16.0")])]})});
            var Q4;
            Q4=makeQuery(id+"F33.opExtrude","SWEPT_BODY",BODY,{"disambiguationData":[OSD([sQuery(id+"F32.wireOp",EDGE,"E56.0"),sQuery(id+"F32.wireOp",EDGE,"E57.0"),sQuery(id+"F32.wireOp",EDGE,"E58.0")])]});
            booleanBodies(context, id + "F35", {"operationType" : BooleanOperationType.SUBTRACTION, "tools" : qUnion([Q0, Q1, Q2, Q3]), "targets" : qUnion([Q4]), "keepTools" : true});
        }
    });
